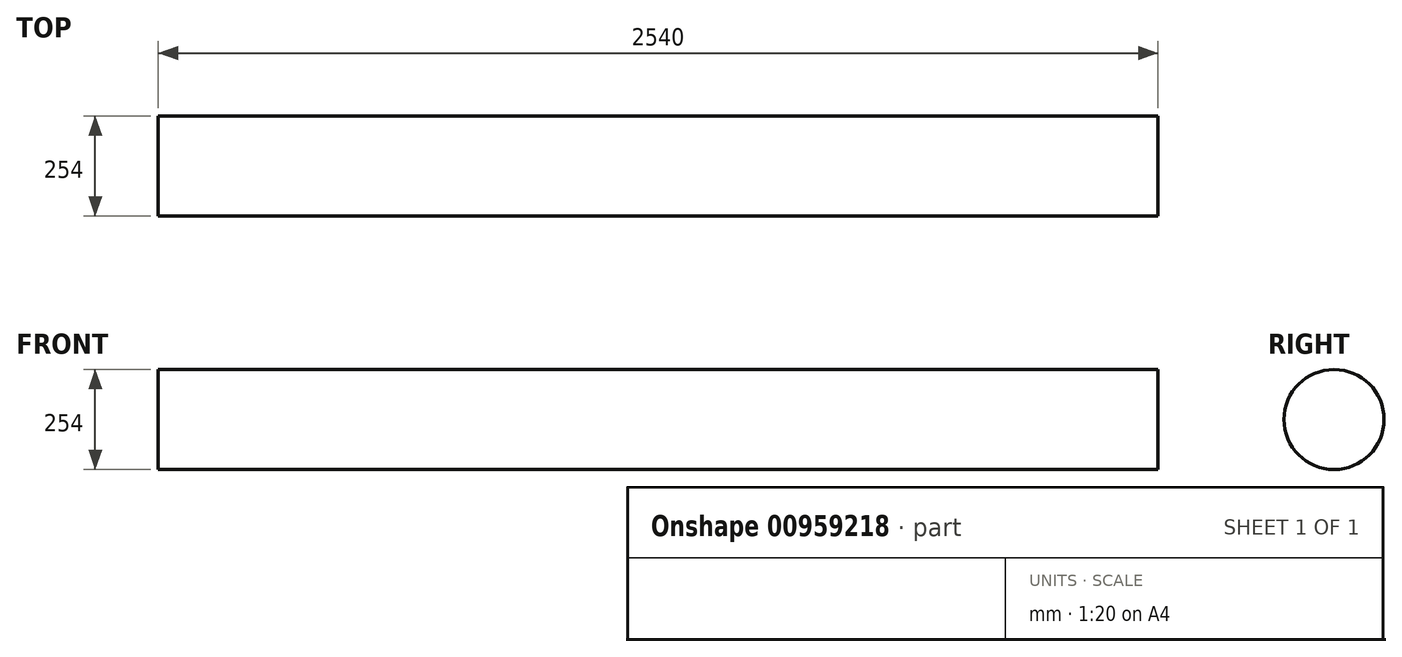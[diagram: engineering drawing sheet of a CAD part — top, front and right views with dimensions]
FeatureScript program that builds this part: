
annotation { "Feature Type Name" : "Feature", "Feature Type Description" : "" }
export const myFeature = defineFeature(function(context is Context, id is Id, definition is map)
    precondition{}
    {
        {
            var Q0;
            Q0=qCreatedBy(makeId("Right.planeOp"),FACE);
            var sketch = newSketch(context, id + "F0", { "sketchPlane" : qUnion([Q0])});
            skCircle(sketch, "E0", {"center": v(0, 0) * mm, "radius": 127 * mm});
            skSolve(sketch);
        }
        {
            var Q0;
            Q0 = qSketchRegion(id + "F0", true);
            extrude(context, id + "F1", {"entities" : qUnion([Q0]), "depth" : 2540 * mm, "offsetDistance" : 25.4 * mm});
        }
    });
